# Revit family: LINESPOT II LED EMERGENCY LIGHT TWS9992WA
name_source: partatom
category: Lighting Fixtures
revit_build: Autodesk Revit 2015 (Build: 20160512_0715(x64)
units: mm (PartAtom-declared; Revit-internal decimal feet)

## types (1)
- TWS9992WA
    Body Material = Plastic
    Color = RAL9003
    Color Filter = 16777215
    Depth = 180 mm  [stored 0.590551 ft]
    Dimming Lamp Color Temperature Shift = <None>
    Height = 50 mm  [stored 0.164042 ft]
    Keynote = 23
    Light Source Symbol Length = 2350 mm
    Manufacturer = Teknoware Oy
    Model = LINESPOT/ZONESPOT II SURFACE
    Product Code = TWS9992WA
    Spot Beam Angle = 30.00°
    Spot Field Angle = 90.00°
    Tilt Angle = 90.00°
    Type Image = <None>
    Width = 180 mm  [stored 0.590551 ft]

note: [stored X ft] marks values corroborated as IEEE doubles in the binary element streams (Revit-internal decimal feet)

## geometry (parser evidence)
native form markers: Blend x6, Sweep x6
no freeform markers — native parametric forms only
